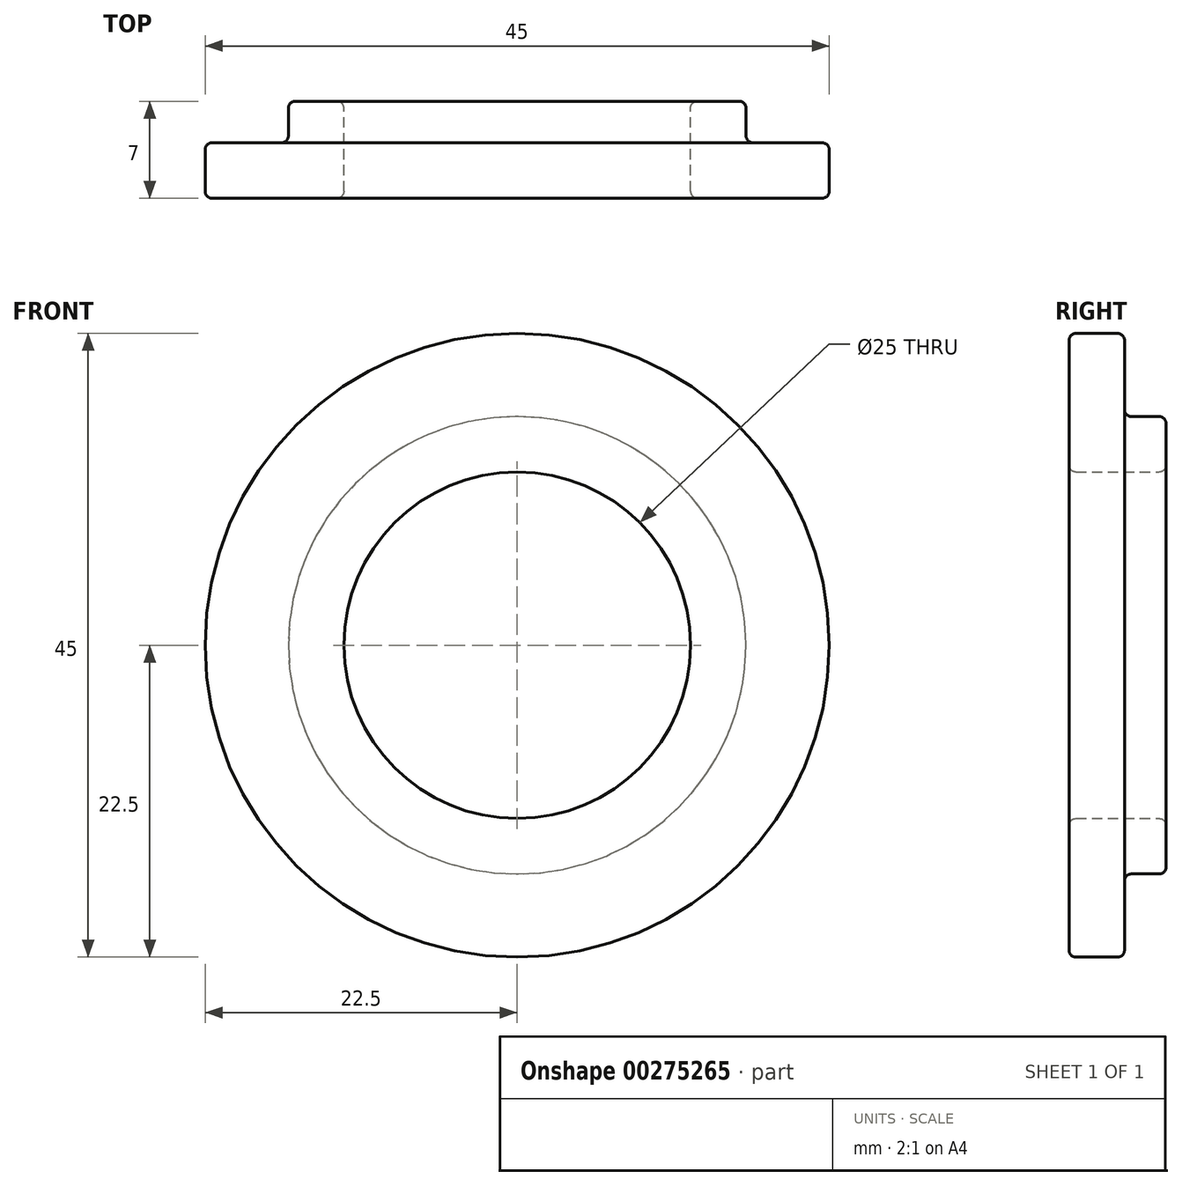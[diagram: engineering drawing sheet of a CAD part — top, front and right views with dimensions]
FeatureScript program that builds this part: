
annotation { "Feature Type Name" : "Feature", "Feature Type Description" : "" }
export const myFeature = defineFeature(function(context is Context, id is Id, definition is map)
    precondition{}
    {
        {
            var Q0;
            Q0=qCreatedBy(makeId("Front.planeOp"),FACE);
            var sketch = newSketch(context, id + "F0", { "sketchPlane" : qUnion([Q0])});
            skCircle(sketch, "E0", {"center": v(0, 0) * mm, "radius": 22.5 * mm});
            skCircle(sketch, "E1", {"center": v(0, 0) * mm, "radius": 12.5 * mm});
            skSolve(sketch);
        }
        {
            var Q0;
            Q0=makeQuery(id+"F0.imprint","IMPRINT",FACE,{"disambiguationData":[TD([[makeQuery(id+"F0.imprint","IMPRINT",EDGE,{"derivedFrom":sQuery(id+"F0.wireOp",EDGE,"E0")}),1.0]])]});
            extrude(context, id + "F1", {"entities" : qUnion([Q0]), "depth" : 4 * mm});
        }
        {
            var Q0;
            Q0=makeQuery(id+"F1.opExtrude","CAP_FACE",FACE,{"disambiguationData":[OSD([sQuery(id+"F0.wireOp",EDGE,"E0"),sQuery(id+"F0.wireOp",EDGE,"E1")])],"isStart":true});
            var sketch = newSketch(context, id + "F2", { "sketchPlane" : qUnion([Q0])});
            skCircle(sketch, "E2", {"center": v(0, 0) * mm, "radius": 16.5 * mm});
            skCircle(sketch, "E3.0", {"center": v(0, 0) * mm, "radius": 12.5 * mm});
            skSolve(sketch);
        }
        {
            var Q0;
            Q0=makeQuery(id+"F2.imprint","IMPRINT",FACE,{"disambiguationData":[TD([[makeQuery(id+"F2.imprint","IMPRINT",EDGE,{"derivedFrom":sQuery(id+"F2.wireOp",EDGE,"E2")}),1.0]])]});
            extrude(context, id + "F3", {"entities" : qUnion([Q0]), "operationType" : NewBodyOperationType.ADD, "depth" : 3 * mm});
        }
        {
            var Q0;
            Q0=makeQuery(id+"F1.opExtrude","CAP_FACE",FACE,{"disambiguationData":[OSD([sQuery(id+"F0.wireOp",EDGE,"E0"),sQuery(id+"F0.wireOp",EDGE,"E1")])],"isStart":false});
            var Q1;
            Q1=makeQuery(id+"F1.opExtrude","CAP_FACE",FACE,{"disambiguationData":[OSD([sQuery(id+"F0.wireOp",EDGE,"E0"),sQuery(id+"F0.wireOp",EDGE,"E1")])],"isStart":true});
            var Q2;
            Q2=makeQuery(id+"F3.opExtrude","CAP_EDGE",EDGE,{"disambiguationData":[OSD([sQuery(id+"F2.wireOp",EDGE,"E2")])],"isStart":false});
            fillet(context, id + "F4", {"entities" : qUnion([Q0, Q1, Q2]), "radius" : .5 * mm, "tangentPropagation" : true, "allowEdgeOverflow" : false});
        }
        {
            var Q0;
            Q0=makeQuery(id+"F3.opExtrude","CAP_EDGE",EDGE,{"disambiguationData":[OSD([sQuery(id+"F2.wireOp",EDGE,"E3.0")])],"isStart":false});
            fillet(context, id + "F5", {"entities" : qUnion([Q0]), "radius" : .5 * mm, "tangentPropagation" : true, "allowEdgeOverflow" : false});
        }
    });
